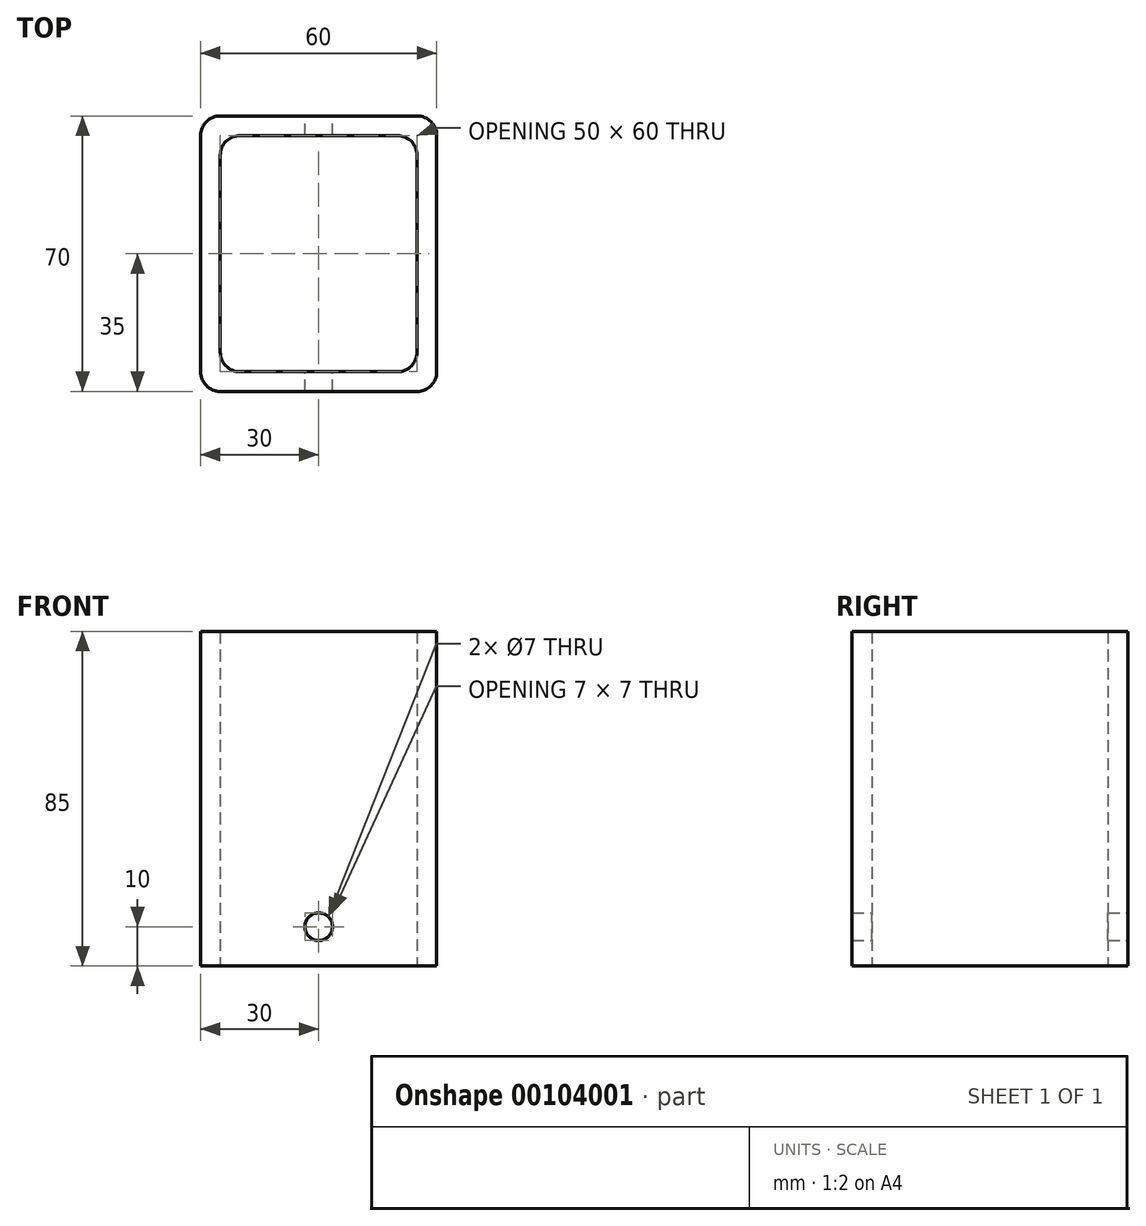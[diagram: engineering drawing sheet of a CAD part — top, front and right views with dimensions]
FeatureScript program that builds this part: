
annotation { "Feature Type Name" : "Feature", "Feature Type Description" : "" }
export const myFeature = defineFeature(function(context is Context, id is Id, definition is map)
    precondition{}
    {
        {
            var Q0;
            Q0=qCreatedBy(makeId("Top.planeOp"),FACE);
            var sketch = newSketch(context, id + "F0", { "sketchPlane" : qUnion([Q0])});
            skLineSegment(sketch, "E0.bottom", {"start": v(25, 30) * mm, "end": v(-25, 30) * mm});
            skLineSegment(sketch, "E0.top", {"start": v(25, -30) * mm, "end": v(-25, -30) * mm});
            skLineSegment(sketch, "E0.left", {"start": v(25, 30) * mm, "end": v(25, -30) * mm});
            skLineSegment(sketch, "E0.right", {"start": v(-25, 30) * mm, "end": v(-25, -30) * mm});
            skPoint(sketch, "E0.middle", {"position": v(0, 0) * mm});
            skLineSegment(sketch, "E1.bottom", {"start": v(30, 35) * mm, "end": v(-30, 35) * mm});
            skLineSegment(sketch, "E1.top", {"start": v(30, -35) * mm, "end": v(-30, -35) * mm});
            skLineSegment(sketch, "E1.left", {"start": v(30, 35) * mm, "end": v(30, -35) * mm});
            skLineSegment(sketch, "E1.right", {"start": v(-30, 35) * mm, "end": v(-30, -35) * mm});
            skSolve(sketch);
        }
        {
            var Q0;
            Q0 = qSketchRegion(id + "F0", true);
            extrude(context, id + "F1", {"entities" : qUnion([Q0]), "depth" : 25 * mm});
        }
        {
            var Q0;
            Q0=makeQuery(id+"F1.opExtrude","CAP_FACE",FACE,{"disambiguationData":[OSD([sQuery(id+"F0.wireOp",EDGE,"E0.bottom"),sQuery(id+"F0.wireOp",EDGE,"E0.top"),sQuery(id+"F0.wireOp",EDGE,"E0.left"),sQuery(id+"F0.wireOp",EDGE,"E0.right"),sQuery(id+"F0.wireOp",EDGE,"E1.bottom"),sQuery(id+"F0.wireOp",EDGE,"E1.top"),sQuery(id+"F0.wireOp",EDGE,"E1.left"),sQuery(id+"F0.wireOp",EDGE,"E1.right")])],"isStart":false});
            extrude(context, id + "F2", {"entities" : qUnion([Q0]), "operationType" : NewBodyOperationType.ADD, "depth" : 60 * mm});
        }
        {
            var Q0;
            {var subQ0=sQuery(id+"F0.wireOp",EDGE,"E0.left");var subQ1=sQuery(id+"F0.wireOp",EDGE,"E0.bottom");Q0=makeQuery(id+"F2.boolean.opBoolean","MERGE",EDGE,{"derivedFrom":[makeQuery(id+"F1.opExtrude","SWEPT_EDGE",EDGE,{"disambiguationData":[OSD([subQ1,subQ0])]}),makeQuery(id+"F2.opExtrude","SWEPT_EDGE",EDGE,{"disambiguationData":[OSD([subQ1,subQ0])]})]});}
            var Q1;
            {var subQ0=sQuery(id+"F0.wireOp",EDGE,"E1.left");var subQ1=sQuery(id+"F0.wireOp",EDGE,"E1.top");Q1=makeQuery(id+"F2.boolean.opBoolean","MERGE",EDGE,{"derivedFrom":[makeQuery(id+"F1.opExtrude","SWEPT_EDGE",EDGE,{"disambiguationData":[OSD([subQ1,subQ0])]}),makeQuery(id+"F2.opExtrude","SWEPT_EDGE",EDGE,{"disambiguationData":[OSD([subQ1,subQ0])]})]});}
            var Q2;
            {var subQ0=sQuery(id+"F0.wireOp",EDGE,"E1.right");var subQ1=sQuery(id+"F0.wireOp",EDGE,"E1.top");Q2=makeQuery(id+"F2.boolean.opBoolean","MERGE",EDGE,{"derivedFrom":[makeQuery(id+"F1.opExtrude","SWEPT_EDGE",EDGE,{"disambiguationData":[OSD([subQ1,subQ0])]}),makeQuery(id+"F2.opExtrude","SWEPT_EDGE",EDGE,{"disambiguationData":[OSD([subQ1,subQ0])]})]});}
            var Q3;
            {var subQ0=sQuery(id+"F0.wireOp",EDGE,"E1.right");var subQ1=sQuery(id+"F0.wireOp",EDGE,"E1.bottom");Q3=makeQuery(id+"F2.boolean.opBoolean","MERGE",EDGE,{"derivedFrom":[makeQuery(id+"F1.opExtrude","SWEPT_EDGE",EDGE,{"disambiguationData":[OSD([subQ1,subQ0])]}),makeQuery(id+"F2.opExtrude","SWEPT_EDGE",EDGE,{"disambiguationData":[OSD([subQ1,subQ0])]})]});}
            var Q4;
            {var subQ0=sQuery(id+"F0.wireOp",EDGE,"E1.left");var subQ1=sQuery(id+"F0.wireOp",EDGE,"E1.bottom");Q4=makeQuery(id+"F2.boolean.opBoolean","MERGE",EDGE,{"derivedFrom":[makeQuery(id+"F1.opExtrude","SWEPT_EDGE",EDGE,{"disambiguationData":[OSD([subQ1,subQ0])]}),makeQuery(id+"F2.opExtrude","SWEPT_EDGE",EDGE,{"disambiguationData":[OSD([subQ1,subQ0])]})]});}
            var Q5;
            {var subQ0=sQuery(id+"F0.wireOp",EDGE,"E0.left");var subQ1=sQuery(id+"F0.wireOp",EDGE,"E0.top");Q5=makeQuery(id+"F2.boolean.opBoolean","MERGE",EDGE,{"derivedFrom":[makeQuery(id+"F1.opExtrude","SWEPT_EDGE",EDGE,{"disambiguationData":[OSD([subQ1,subQ0])]}),makeQuery(id+"F2.opExtrude","SWEPT_EDGE",EDGE,{"disambiguationData":[OSD([subQ1,subQ0])]})]});}
            var Q6;
            {var subQ0=sQuery(id+"F0.wireOp",EDGE,"E0.right");var subQ1=sQuery(id+"F0.wireOp",EDGE,"E0.bottom");Q6=makeQuery(id+"F2.boolean.opBoolean","MERGE",EDGE,{"derivedFrom":[makeQuery(id+"F1.opExtrude","SWEPT_EDGE",EDGE,{"disambiguationData":[OSD([subQ1,subQ0])]}),makeQuery(id+"F2.opExtrude","SWEPT_EDGE",EDGE,{"disambiguationData":[OSD([subQ1,subQ0])]})]});}
            var Q7;
            {var subQ0=sQuery(id+"F0.wireOp",EDGE,"E0.right");var subQ1=sQuery(id+"F0.wireOp",EDGE,"E0.top");Q7=makeQuery(id+"F2.boolean.opBoolean","MERGE",EDGE,{"derivedFrom":[makeQuery(id+"F1.opExtrude","SWEPT_EDGE",EDGE,{"disambiguationData":[OSD([subQ1,subQ0])]}),makeQuery(id+"F2.opExtrude","SWEPT_EDGE",EDGE,{"disambiguationData":[OSD([subQ1,subQ0])]})]});}
            fillet(context, id + "F3", {"entities" : qUnion([Q0, Q1, Q2, Q3, Q4, Q5, Q6, Q7]), "radius" : 5 * mm, "tangentPropagation" : true, "allowEdgeOverflow" : false});
        }
        {
            var Q0;
            {var subQ0=sQuery(id+"F0.wireOp",EDGE,"E1.bottom");Q0=makeQuery(id+"F2.boolean.opBoolean","MERGE",FACE,{"derivedFrom":[makeQuery(id+"F1.opExtrude","SWEPT_FACE",FACE,{"disambiguationData":[OSD([subQ0])]}),makeQuery(id+"F2.opExtrude","SWEPT_FACE",FACE,{"disambiguationData":[OSD([subQ0])]})]});}
            var sketch = newSketch(context, id + "F4", { "sketchPlane" : qUnion([Q0])});
            skCircle(sketch, "E2", {"center": v(0, 10) * mm, "radius": 3.5 * mm});
            skSolve(sketch);
        }
        {
            var Q0;
            Q0=makeQuery(id+"F4.imprint","IMPRINT",FACE,{"disambiguationData":[TD([[makeQuery(id+"F4.imprint","IMPRINT",EDGE,{"derivedFrom":sQuery(id+"F4.wireOp",EDGE,"E2")}),1.0]])]});
            extrude(context, id + "F5", {"entities" : qUnion([Q0]), "operationType" : NewBodyOperationType.REMOVE, "oppositeDirection" : true, "depth" : 70 * mm});
        }
    });
